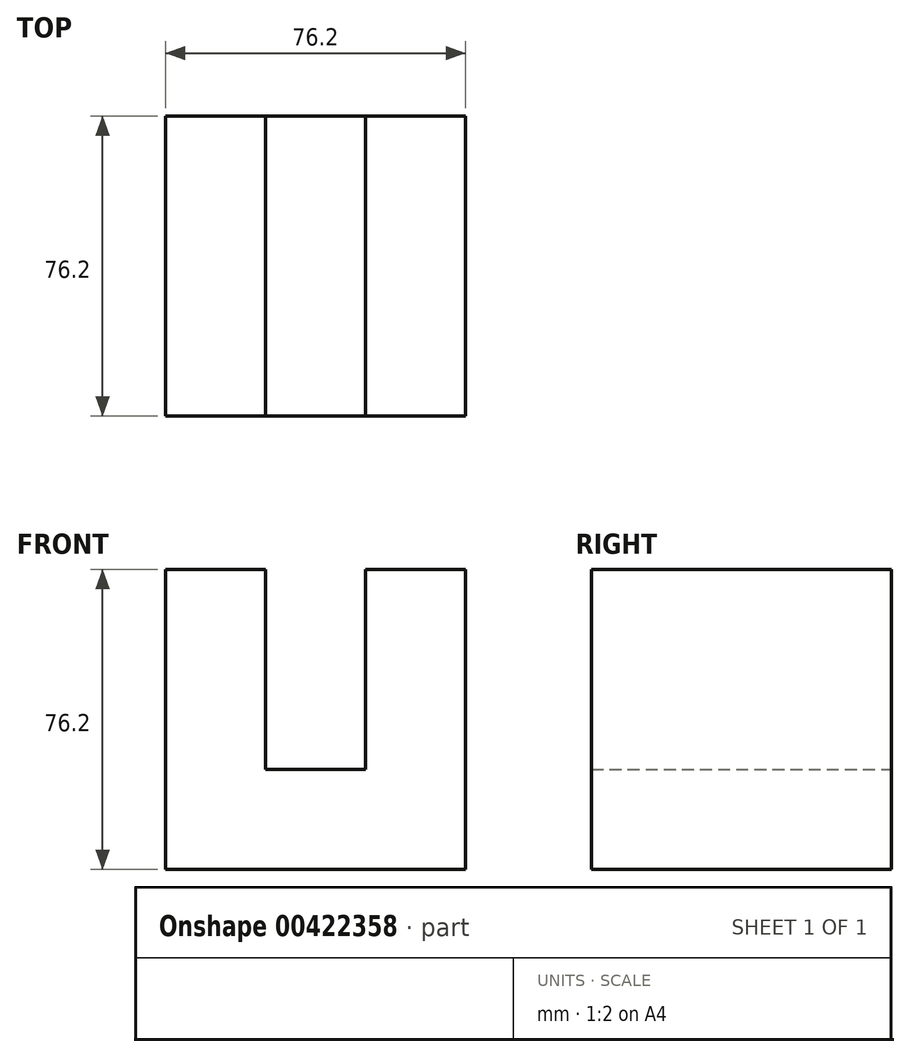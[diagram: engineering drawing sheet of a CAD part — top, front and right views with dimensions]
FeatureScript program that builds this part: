
annotation { "Feature Type Name" : "Feature", "Feature Type Description" : "" }
export const myFeature = defineFeature(function(context is Context, id is Id, definition is map)
    precondition{}
    {
        {
            var Q0;
            Q0=qCreatedBy(makeId("Front.planeOp"),FACE);
            var sketch = newSketch(context, id + "F0", { "sketchPlane" : qUnion([Q0])});
            skLineSegment(sketch, "E0", {"start": v(-50.8, 76.2) * mm, "end": v(-50.8, 0) * mm});
            skLineSegment(sketch, "E1", {"start": v(-50.8, 0) * mm, "end": v(25.4, 0) * mm});
            skLineSegment(sketch, "E2", {"start": v(-50.8, 76.2) * mm, "end": v(-25.4, 76.2) * mm});
            skLineSegment(sketch, "E3", {"start": v(-25.4, 76.2) * mm, "end": v(-25.4, 25.4) * mm});
            skLineSegment(sketch, "E4", {"start": v(25.4, 0) * mm, "end": v(25.4, 76.2) * mm});
            skLineSegment(sketch, "E5", {"start": v(25.4, 76.2) * mm, "end": v(0, 76.2) * mm});
            skLineSegment(sketch, "E6", {"start": v(0, 76.2) * mm, "end": v(0, 25.4) * mm});
            skLineSegment(sketch, "E7", {"start": v(-25.4, 25.4) * mm, "end": v(0, 25.4) * mm});
            skLineSegment(sketch, "E8", {"start": v(8.87, 13.1) * mm, "end": v(8.87, 9.59) * mm});
            skSolve(sketch);
        }
        {
            var Q0;
            Q0 = qSketchRegion(id + "F0", true);
            extrude(context, id + "F1", {"entities" : qUnion([Q0]), "depth" : 76.2 * mm});
        }
    });
